# Revit family: Hager-Panelboard_Invicta_3_250A-NoHosted-UK-en
name_source: partatom
category: Electrical Equipment
units: mm (PartAtom-declared; Revit-internal decimal feet)

## family parameters
Always vertical = Yes
Cut with Voids When Loaded = No
Panel Configuration = Two Columns, Circuits Across
Part Type = Panelboard
Room Calculation Point = No
Round Connector Dimension = Use Diameter
Shared = No
Work Plane-Based = Yes

## types (9) — shared parameters
Classification.Uniclass.Pr.Description = Control circuit device enclosures
Classification.Uniclass.Pr.Number = Pr_80_77_28_16
Default Elevation = 1219 mm
EF000003 - Mounting method = EV000384 - Surface mounted (plaster)
EF000008 - Width = 710 mm  [stored 2.3294 ft]
EF000049 - Depth = 178 mm  [stored 0.58399 ft]
EF000118 - With mounting plate = No
EF001062 - EMC-version = No
EF001088 - Extension possible = No
EF001134 - DIN-rail = No
EF004462 - Type of closure = EV000154 - Other
EF005474 - Degree of protection (IP) = EV006410 - IP30
EF006306 - With lock = No
EF015941 - Signal passing door = No
HG000002 - With door or cover = Yes
HG000003 - Range = Panelboards
HG000005 - Thickness = 3 mm  [stored 0.00984252 ft]
HG000017 - Distance between poles = 25 mm  [stored 0.082021 ft]
Manufacturer = Hager
Type Comments = Panelboards
zero-valued in all types: EF000218 - Built-in depth, EF000266 - Number of rows, EF000332 - Built-in height, EF000846 - Built-in width, EF001131 - Internal depth

## per-type parameters (varying)
| type | EF000007 - Colour | EF000040 - Height | EF000116 - RAL-number | EF000339 - Type of cover | EF001596 - Material housing | EF002950 - Width in number of modular spacings | EF006244 - Transparent cover/door | EF015776 - Earthing terminal block | EF015777 - Neutral terminal block | HG000004 - Manufacturer reference | Model |
| Surface mounted IP30 W710 H1100 D178.4 12 Modular spacings - JN208B | EV000154 - Other | 1100 mm | 9001 | EV004216 - Door | EV000179 - Steel | 12 | No | Yes | Yes | JN208B | JN208B |
| Surface mounted IP30 W710 H1100 D178.4 12 Modular spacings - JN208BG |  | 1100 mm |  | EV001012 - Cover |  | 12 | Yes | No | No | JN208BG | JN208BG |
| Surface mounted IP30 W710 H1100 D178.4 9 Modular spacings - JN206B | EV000154 - Other | 1100 mm | 9001 | EV004216 - Door | EV000179 - Steel | 9 | No | Yes | Yes | JN206B | JN206B |
| Surface mounted IP30 W710 H1100 D178.4 9 Modular spacings - JN206BG |  | 1100 mm |  | EV004216 - Door | EV000179 - Steel | 9 | Yes | Yes | Yes | JN206BG | JN206BG |
| Surface mounted IP30 W710 H1250 D178.4 18 Modular spacings - JN212BG | EV000154 - Other | 1250 mm  [stored 4.10105 ft] | 9001 | EV004216 - Door | EV000179 - Steel | 18 | Yes | Yes | Yes | JN212BG | JN212BG |
| Surface mounted IP30 W710 H1550 D178.4 24 Modular spacings - JN216B | EV000154 - Other | 1550 mm | 9001 | EV004216 - Door | EV000179 - Steel | 24 | No | Yes | Yes | JN216B | JN216B |
| Surface mounted IP30 W710 H1550 D178.4 24 Modular spacings - JN216BG | EV000154 - Other | 1550 mm | 9001 | EV001012 - Cover | EV000179 - Steel | 24 | Yes | Yes | Yes | JN216BG | JN216BG |
| Surface mounted IP30 W710 H950 D178.4 6 Modular spacings - JN204B | EV000154 - Other | 950 mm  [stored 3.1168 ft] | 9001 | EV004216 - Door | EV000179 - Steel | 6 | No | Yes | Yes | JN204B | JN204B |
| Surface mounted IP30 W710 H950 D178.4 6 Modular spacings - JN204BG | EV000154 - Other | 950 mm  [stored 3.1168 ft] | 9001 | EV001012 - Cover | EV000179 - Steel | 6 | Yes | Yes | Yes | JN204BG | JN204BG |

note: [stored X ft] marks values corroborated as IEEE doubles in the binary element streams (Revit-internal decimal feet)

## geometry (parser evidence)
native form markers: Sweep x12
no freeform markers — native parametric forms only
